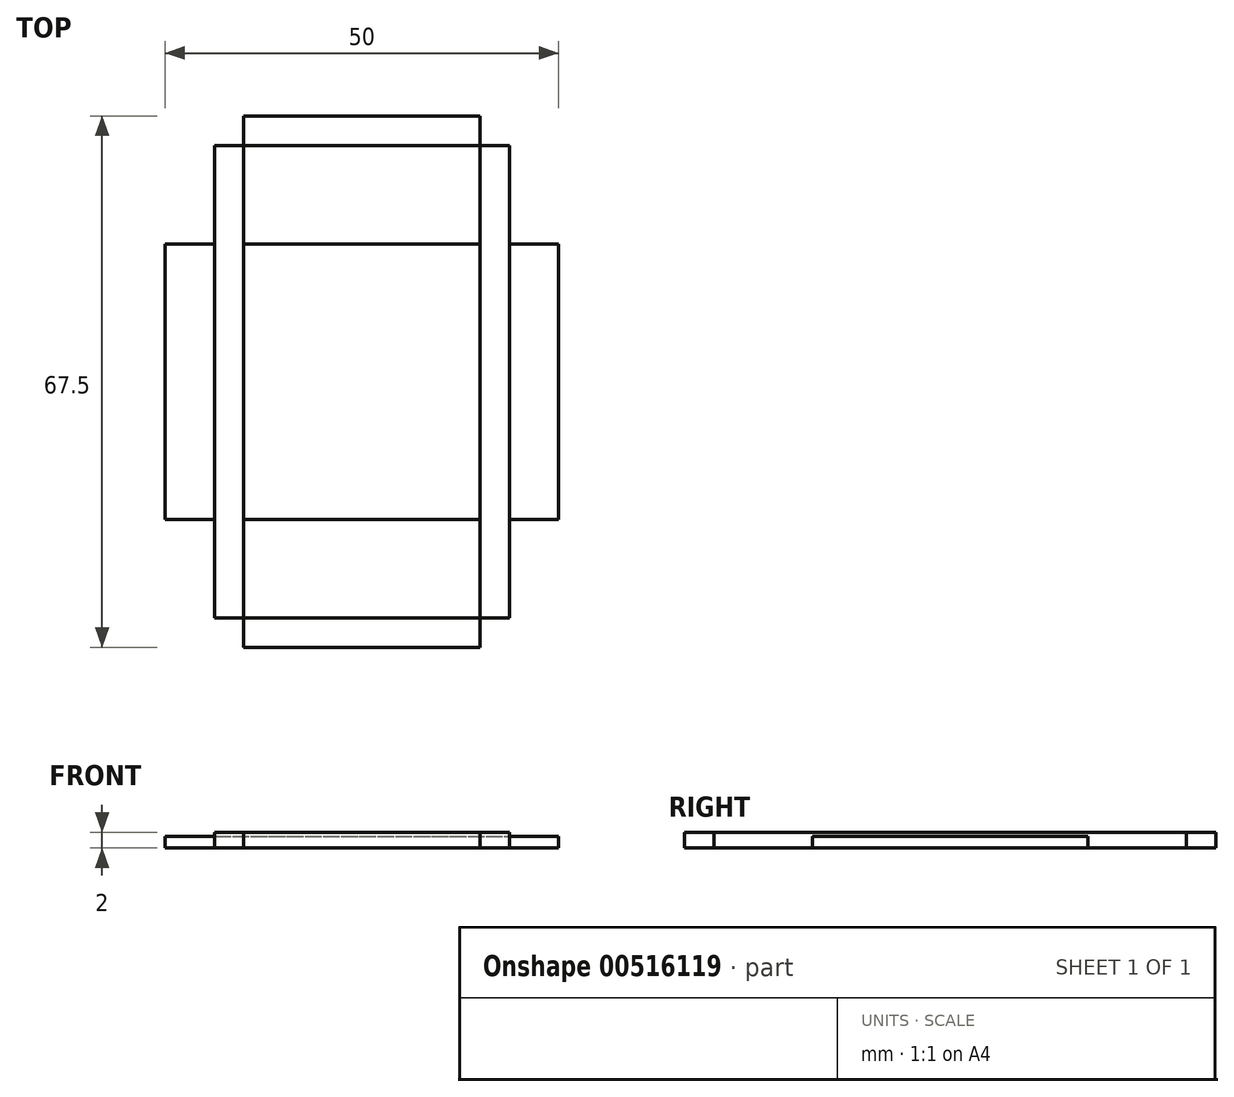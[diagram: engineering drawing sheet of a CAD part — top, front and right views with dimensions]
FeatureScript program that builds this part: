
annotation { "Feature Type Name" : "Feature", "Feature Type Description" : "" }
export const myFeature = defineFeature(function(context is Context, id is Id, definition is map)
    precondition{}
    {
        {
            var Q0;
            Q0=qCreatedBy(makeId("Top.planeOp"),FACE);
            var sketch = newSketch(context, id + "F0", { "sketchPlane" : qUnion([Q0])});
            skLineSegment(sketch, "E0.bottom", {"start": v(15, 17.5) * mm, "end": v(-15, 17.5) * mm});
            skLineSegment(sketch, "E0.top", {"start": v(15, -17.5) * mm, "end": v(-15, -17.5) * mm});
            skLineSegment(sketch, "E0.left", {"start": v(15, 17.5) * mm, "end": v(15, -17.5) * mm});
            skLineSegment(sketch, "E0.right", {"start": v(-15, 17.5) * mm, "end": v(-15, -17.5) * mm});
            skPoint(sketch, "E0.middle", {"position": v(0, 0) * mm});
            skSolve(sketch);
        }
        {
            var Q0;
            Q0=makeQuery(id+"F0.imprint","IMPRINT",FACE,{"disambiguationData":[TD([[makeQuery(id+"F0.imprint","IMPRINT",EDGE,{"derivedFrom":sQuery(id+"F0.wireOp",EDGE,"E0.bottom")}),1.0]])]});
            extrude(context, id + "F1", {"entities" : qUnion([Q0]), "depth" : 2 * mm, "offsetDistance" : 25 * mm});
        }
        {
            var Q0;
            Q0=qCreatedBy(makeId("Top.planeOp"),FACE);
            var sketch = newSketch(context, id + "F2", { "sketchPlane" : qUnion([Q0])});
            skLineSegment(sketch, "E1.bottom", {"start": v(-15, 33.75) * mm, "end": v(15, 33.75) * mm});
            skLineSegment(sketch, "E1.top", {"start": v(-15, -33.75) * mm, "end": v(15, -33.75) * mm});
            skLineSegment(sketch, "E1.left", {"start": v(-15, 33.75) * mm, "end": v(-15, -33.75) * mm});
            skLineSegment(sketch, "E1.right", {"start": v(15, 33.75) * mm, "end": v(15, -33.75) * mm});
            skPoint(sketch, "E1.middle", {"position": v(0, 0) * mm});
            skSolve(sketch);
        }
        {
            var Q0;
            Q0=makeQuery(id+"F2.imprint","IMPRINT",FACE,{"disambiguationData":[TD([[makeQuery(id+"F2.imprint","IMPRINT",EDGE,{"derivedFrom":sQuery(id+"F2.wireOp",EDGE,"E1.bottom")}),-1.0]])]});
            extrude(context, id + "F3", {"entities" : qUnion([Q0]), "depth" : 2 * mm, "offsetDistance" : 25 * mm});
        }
        {
            var Q0;
            Q0=qCreatedBy(makeId("Top.planeOp"),FACE);
            var sketch = newSketch(context, id + "F4", { "sketchPlane" : qUnion([Q0])});
            skLineSegment(sketch, "E2.bottom", {"start": v(-25, 17.5) * mm, "end": v(25, 17.5) * mm});
            skLineSegment(sketch, "E2.top", {"start": v(-25, -17.5) * mm, "end": v(25, -17.5) * mm});
            skLineSegment(sketch, "E2.left", {"start": v(-25, 17.5) * mm, "end": v(-25, -17.5) * mm});
            skLineSegment(sketch, "E2.right", {"start": v(25, 17.5) * mm, "end": v(25, -17.5) * mm});
            skPoint(sketch, "E2.middle", {"position": v(0, 0) * mm});
            skSolve(sketch);
        }
        {
            var Q0;
            Q0=makeQuery(id+"F4.imprint","IMPRINT",FACE,{"disambiguationData":[TD([[makeQuery(id+"F4.imprint","IMPRINT",EDGE,{"derivedFrom":sQuery(id+"F4.wireOp",EDGE,"E2.bottom")}),-1.0]])]});
            extrude(context, id + "F5", {"entities" : qUnion([Q0]), "depth" : 1.5 * mm, "offsetDistance" : 25 * mm});
        }
        {
            var Q0;
            Q0=qCreatedBy(makeId("Top.planeOp"),FACE);
            var sketch = newSketch(context, id + "F6", { "sketchPlane" : qUnion([Q0])});
            skLineSegment(sketch, "E3.bottom", {"start": v(-18.73, 30) * mm, "end": v(18.73, 30) * mm});
            skLineSegment(sketch, "E3.top", {"start": v(-18.73, -30) * mm, "end": v(18.73, -30) * mm});
            skLineSegment(sketch, "E3.left", {"start": v(-18.73, 30) * mm, "end": v(-18.73, -30) * mm});
            skLineSegment(sketch, "E3.right", {"start": v(18.73, 30) * mm, "end": v(18.73, -30) * mm});
            skPoint(sketch, "E3.middle", {"position": v(0, 0) * mm});
            skSolve(sketch);
        }
        {
            var Q0;
            Q0=makeQuery(id+"F6.imprint","IMPRINT",FACE,{"disambiguationData":[TD([[makeQuery(id+"F6.imprint","IMPRINT",EDGE,{"derivedFrom":sQuery(id+"F6.wireOp",EDGE,"E3.bottom")}),-1.0]])]});
            extrude(context, id + "F7", {"entities" : qUnion([Q0]), "depth" : 2 * mm, "offsetDistance" : 25 * mm});
        }
    });
